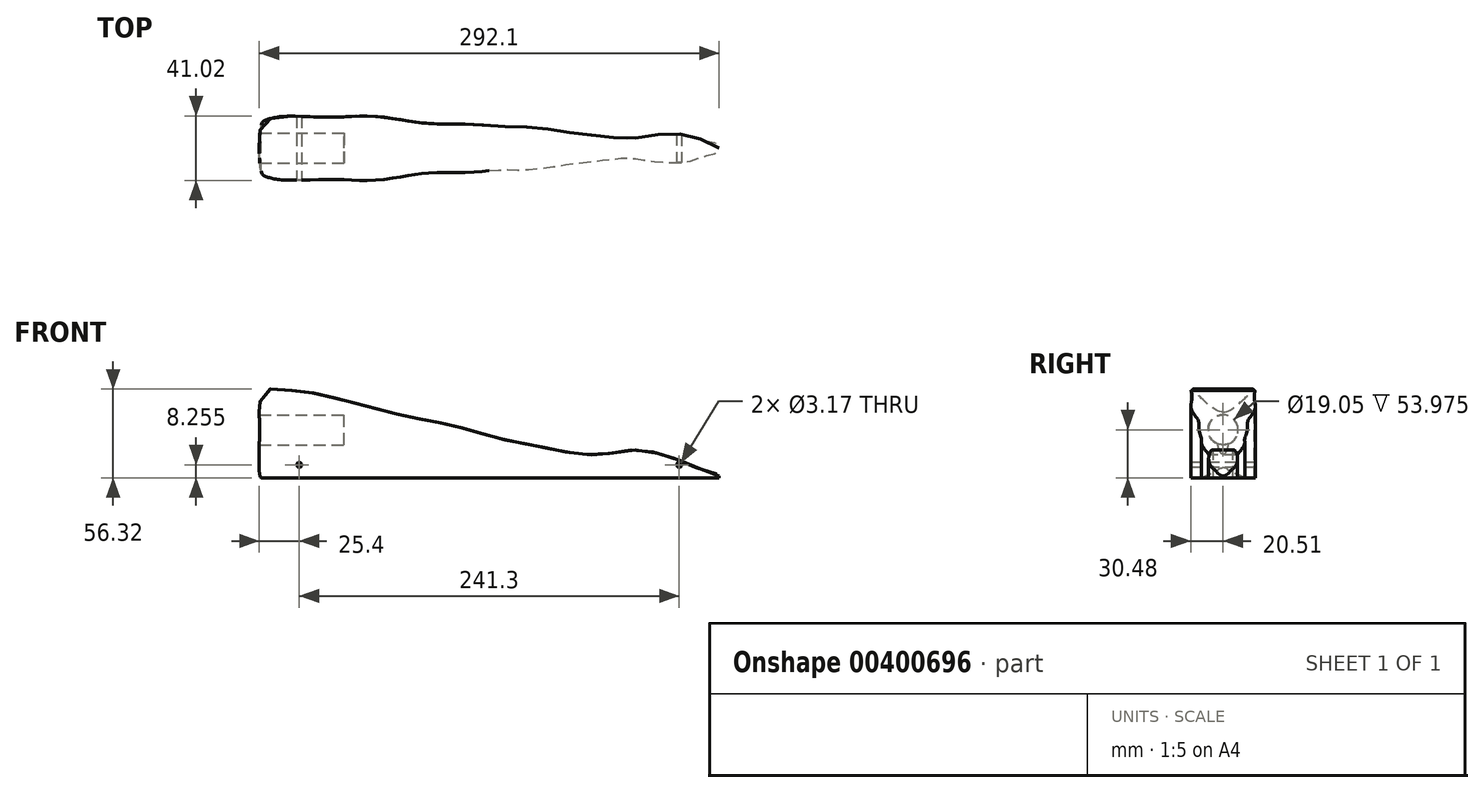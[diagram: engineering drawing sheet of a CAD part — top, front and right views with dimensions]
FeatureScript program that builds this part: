
annotation { "Feature Type Name" : "Feature", "Feature Type Description" : "" }
export const myFeature = defineFeature(function(context is Context, id is Id, definition is map)
    precondition{}
    {
        {
            var Q0;
            Q0=qCreatedBy(makeId("Front.planeOp"),FACE);
            var sketch = newSketch(context, id + "F0", { "sketchPlane" : qUnion([Q0])});
            skLineSegment(sketch, "E0.bottom", {"start": v(-146.05, 31.75) * mm, "end": v(146.05, 31.75) * mm, "construction": true});
            skLineSegment(sketch, "E0.top", {"start": v(-146.05, -31.75) * mm, "end": v(146.05, -31.75) * mm, "construction": true});
            skLineSegment(sketch, "E0.right", {"start": v(146.05, 31.75) * mm, "end": v(146.05, -31.75) * mm, "construction": true});
            skFitSpline(sketch, "E1", {"points": [v(-146.05, -24.02) * mm, v(-146.05, 0) * mm, v(-144.44, 22.2) * mm, v(-140.16, 25.77) * mm, v(-133.2, 25.06) * mm, v(-121.08, 24.7) * mm, v(-100.4, 20.78) * mm, v(-77.92, 15.07) * mm, v(-51.7, 8.3) * mm, v(-24.06, 2.94) * mm, v(7.68, -5.8) * mm, v(30.15, -10.25) * mm, v(45.3, -13.29) * mm, v(70.63, -15.78) * mm, v(95.24, -12.75) * mm, v(124.49, -20.95) * mm, v(134.3, -24.88) * mm, v(146.05, -29.22) * mm, v(145.59, -31.27) * mm, v(144.47, -31.75) * mm, v(115.4, -31.75) * mm, v(90.89, -31.75) * mm, v(68.29, -31.75) * mm, v(46.65, -31.75) * mm, v(19.14, -31.75) * mm, v(-6.96, -31.75) * mm, v(-28.04, -31.75) * mm, v(-58.88, -31.75) * mm, v(-90.58, -31.75) * mm, v(-109.96, -31.75) * mm, v(-137.5, -31.75) * mm, v(-144.78, -30.62) * mm, v(-146.05, -24.02) * mm]});
            skLineSegment(sketch, "E2.bottom", {"start": v(-146.05, 9.52) * mm, "end": v(-95.25, 9.52) * mm, "construction": true});
            skLineSegment(sketch, "E2.top", {"start": v(-141.83, -9.52) * mm, "end": v(-95.25, -9.52) * mm, "construction": true});
            skLineSegment(sketch, "E2.right", {"start": v(-95.25, 9.52) * mm, "end": v(-95.25, -9.52) * mm, "construction": true});
            skLineSegment(sketch, "E3", {"start": v(-146.05, 31.75) * mm, "end": v(-146.05, -31.75) * mm, "construction": true});
            skSolve(sketch);
        }
        {
            var Q0;
            Q0=qCreatedBy(makeId("Top.planeOp"),FACE);
            var sketch = newSketch(context, id + "F1", { "sketchPlane" : qUnion([Q0])});
            skLineSegment(sketch, "E4.bottom", {"start": v(-146.05, 22.22) * mm, "end": v(146.05, 22.23) * mm, "construction": true});
            skLineSegment(sketch, "E4.top", {"start": v(-146.05, -22.23) * mm, "end": v(146.05, -22.22) * mm, "construction": true});
            skLineSegment(sketch, "E4.left", {"start": v(-146.05, 22.22) * mm, "end": v(-146.05, -22.23) * mm, "construction": true});
            skLineSegment(sketch, "E4.right", {"start": v(146.05, 22.22) * mm, "end": v(146.05, -22.22) * mm, "construction": true});
            skLineSegment(sketch, "E5", {"start": v(-146.05, 0) * mm, "end": v(146.05, 0) * mm, "construction": true});
            skFitSpline(sketch, "E6", {"points": [v(-146.05, 0) * mm, v(-144.43, 15.84) * mm, v(-141.15, 18.24) * mm, v(-133.08, 20) * mm, v(-117.06, 20.13) * mm, v(-93.86, 19.88) * mm, v(-74.3, 20.41) * mm, v(-52.37, 17.48) * mm, v(-36.7, 15.63) * mm, v(-9.98, 15.2) * mm, v(6.92, 13.73) * mm, v(24.78, 13.53) * mm, v(52.59, 9.9) * mm, v(76.74, 7.1) * mm, v(88.58, 6.18) * mm, v(99.23, 7.56) * mm, v(125.03, 8.73) * mm, v(138.1, 4.73) * mm, v(146.05, 0) * mm], "startDerivative": vector(0, 335.54) * mm, "endDerivative": vector(0, -277.49) * mm});
            skFitSpline(sketch, "E7.MirrorCS", {"points": [v(-146.05, 0) * mm, v(-144.43, -15.84) * mm, v(-141.15, -18.24) * mm, v(-133.08, -20) * mm, v(-117.06, -20.13) * mm, v(-93.86, -19.88) * mm, v(-74.3, -20.41) * mm, v(-52.37, -17.48) * mm, v(-36.7, -15.63) * mm, v(-9.98, -15.2) * mm, v(6.92, -13.73) * mm, v(24.78, -13.53) * mm, v(52.59, -9.9) * mm, v(76.74, -7.1) * mm, v(88.58, -6.18) * mm, v(99.23, -7.56) * mm, v(125.03, -8.73) * mm, v(138.1, -4.73) * mm, v(146.05, 0) * mm], "startDerivative": vector(0, -335.54) * mm, "endDerivative": vector(0, 277.49) * mm});
            skLineSegment(sketch, "E8.MirrorCS", {"start": v(-146.05, -22.23) * mm, "end": v(146.05, -22.23) * mm});
            skSolve(sketch);
        }
        {
            var Q0;
            Q0=qCreatedBy(makeId("Right.planeOp"),FACE);
            var sketch = newSketch(context, id + "F2", { "sketchPlane" : qUnion([Q0])});
            skCircle(sketch, "E9", {"center": v(0, 0) * mm, "radius": 9.53 * mm});
            skSolve(sketch);
        }
        {
            var Q0;
            Q0=qCreatedBy(makeId("Front.planeOp"),FACE);
            var sketch = newSketch(context, id + "F3", { "sketchPlane" : qUnion([Q0])});
            skCircle(sketch, "E10", {"center": v(-120.65, -22.22) * mm, "radius": 1.59 * mm});
            skCircle(sketch, "E11", {"center": v(120.65, -22.23) * mm, "radius": 1.59 * mm});
            skSolve(sketch);
        }
        {
            var Q0;
            Q0=qSketchRegion(id+"F0",true);
            extrude(context, id + "F4", {"entities" : qUnion([Q0]), "depth" : 44.45 * mm, "symmetric" : true});
        }
        {
            var Q0;
            Q0=qSketchRegion(id+"F1",true);
            extrude(context, id + "F5", {"entities" : qUnion([Q0]), "operationType" : NewBodyOperationType.INTERSECT, "oppositeDirection" : true, "depth" : 60.96 * mm, "symmetric" : true});
        }
        {
            var Q0;
            Q0=qSketchRegion(id+"F2",true);
            extrude(context, id + "F6", {"entities" : qUnion([Q0]), "operationType" : NewBodyOperationType.REMOVE, "oppositeDirection" : true, "depth" : 152.4 * mm, "hasSecondDirection" : true, "secondDirectionOppositeDirection" : true, "secondDirectionDepth" : 92.07 * mm});
        }
        {
            var Q0;
            Q0=qSketchRegion(id+"F3",true);
            extrude(context, id + "F7", {"entities" : qUnion([Q0]), "operationType" : NewBodyOperationType.REMOVE, "oppositeDirection" : true, "depth" : 50.8 * mm, "symmetric" : true});
        }
    });
